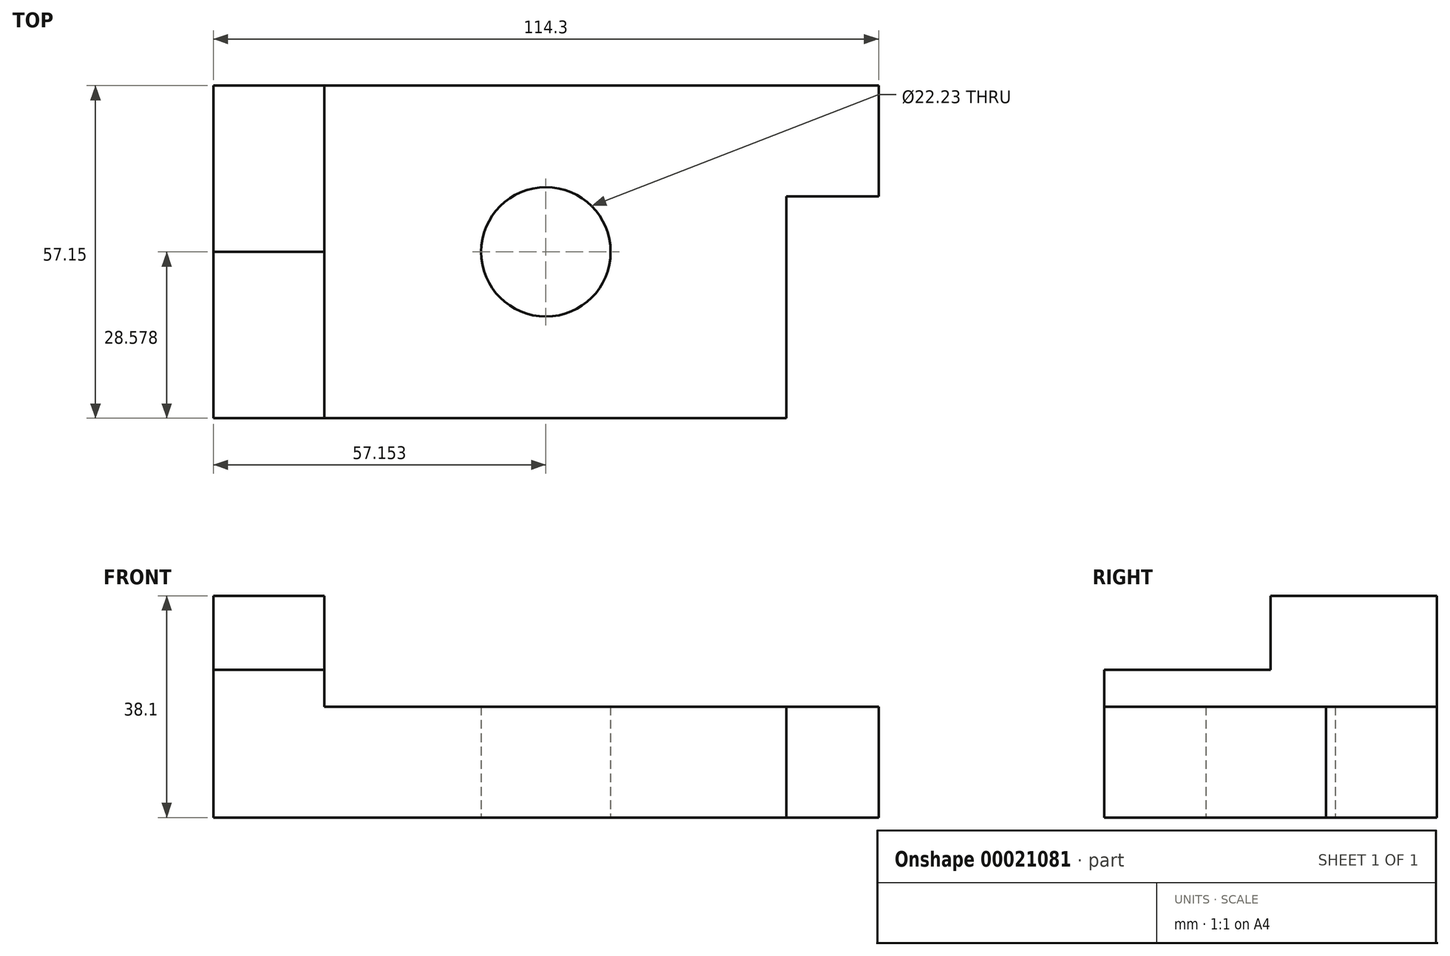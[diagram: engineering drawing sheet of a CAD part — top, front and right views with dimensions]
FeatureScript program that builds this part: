
annotation { "Feature Type Name" : "Feature", "Feature Type Description" : "" }
export const myFeature = defineFeature(function(context is Context, id is Id, definition is map)
    precondition{}
    {
        {
            var Q0;
            Q0=qCreatedBy(makeId("Top.planeOp"),FACE);
            var sketch = newSketch(context, id + "F0", { "sketchPlane" : qUnion([Q0])});
            skLineSegment(sketch, "E0.bottom", {"start": v(-56.1, 26.45) * mm, "end": v(58.2, 26.45) * mm});
            skLineSegment(sketch, "E0.top", {"start": v(-56.1, -30.7) * mm, "end": v(42.32, -30.7) * mm});
            skLineSegment(sketch, "E0.left", {"start": v(-56.1, 26.45) * mm, "end": v(-56.1, -30.7) * mm});
            skLineSegment(sketch, "E0.right", {"start": v(58.2, 26.45) * mm, "end": v(58.2, 7.4) * mm});
            skLineSegment(sketch, "E1.top", {"start": v(58.2, 7.4) * mm, "end": v(42.32, 7.4) * mm});
            skLineSegment(sketch, "E1.right", {"start": v(42.32, -30.7) * mm, "end": v(42.32, 7.4) * mm});
            skCircle(sketch, "E2", {"center": v(1.04, -2.12) * mm, "radius": 11.11 * mm});
            skPoint(sketch, "E3.orphan", {"position": v(58.2, -30.7) * mm});
            skSolve(sketch);
        }
        {
            var Q0;
            Q0 = qSketchRegion(id + "F0", true);
            extrude(context, id + "F1", {"entities" : qUnion([Q0]), "depth" : 38.1 * mm});
        }
        {
            var Q0;
            Q0=makeQuery(id+"F1.opExtrude","CAP_FACE",FACE,{"disambiguationData":[OSD([sQuery(id+"F0.wireOp",EDGE,"E0.bottom"),sQuery(id+"F0.wireOp",EDGE,"E0.top"),sQuery(id+"F0.wireOp",EDGE,"E0.left"),sQuery(id+"F0.wireOp",EDGE,"E0.right"),sQuery(id+"F0.wireOp",EDGE,"E1.top"),sQuery(id+"F0.wireOp",EDGE,"E1.right"),sQuery(id+"F0.wireOp",EDGE,"E2")])],"isStart":false});
            var sketch = newSketch(context, id + "F2", { "sketchPlane" : qUnion([Q0])});
            skLineSegment(sketch, "E4.bottom", {"start": v(-56.1, -30.7) * mm, "end": v(-37.06, -30.7) * mm});
            skLineSegment(sketch, "E4.top", {"start": v(-56.1, -2.12) * mm, "end": v(-37.06, -2.12) * mm});
            skLineSegment(sketch, "E4.left", {"start": v(-56.1, -30.7) * mm, "end": v(-56.1, -2.12) * mm});
            skLineSegment(sketch, "E4.right", {"start": v(-37.06, -30.7) * mm, "end": v(-37.06, -2.12) * mm});
            skSolve(sketch);
        }
        {
            var Q0;
            Q0 = qSketchRegion(id + "F2", true);
            extrude(context, id + "F3", {"entities" : qUnion([Q0]), "operationType" : NewBodyOperationType.REMOVE, "oppositeDirection" : true, "depth" : 12.7 * mm});
        }
        {
            var Q0;
            Q0=makeQuery(id+"F1.opExtrude","CAP_FACE",FACE,{"disambiguationData":[OSD([sQuery(id+"F0.wireOp",EDGE,"E0.bottom"),sQuery(id+"F0.wireOp",EDGE,"E0.top"),sQuery(id+"F0.wireOp",EDGE,"E0.left"),sQuery(id+"F0.wireOp",EDGE,"E0.right"),sQuery(id+"F0.wireOp",EDGE,"E1.top"),sQuery(id+"F0.wireOp",EDGE,"E1.right"),sQuery(id+"F0.wireOp",EDGE,"E2")])],"isStart":false});
            var sketch = newSketch(context, id + "F4", { "sketchPlane" : qUnion([Q0])});
            skLineSegment(sketch, "E5.bottom", {"start": v(58.2, 7.4) * mm, "end": v(42.32, 7.4) * mm});
            skLineSegment(sketch, "E5.top", {"start": v(58.2, 26.45) * mm, "end": v(42.32, 26.45) * mm});
            skLineSegment(sketch, "E5.left", {"start": v(58.2, 7.4) * mm, "end": v(58.2, 26.45) * mm});
            skLineSegment(sketch, "E5.right", {"start": v(42.32, 7.4) * mm, "end": v(42.32, 26.45) * mm});
            skSolve(sketch);
        }
        {
            var Q0;
            Q0 = qSketchRegion(id + "F4", true);
            extrude(context, id + "F5", {"entities" : qUnion([Q0]), "operationType" : NewBodyOperationType.REMOVE, "oppositeDirection" : true, "depth" : 19.05 * mm});
        }
        {
            var Q0;
            Q0=makeQuery(id+"F1.opExtrude","CAP_FACE",FACE,{"disambiguationData":[OSD([sQuery(id+"F0.wireOp",EDGE,"E0.bottom"),sQuery(id+"F0.wireOp",EDGE,"E0.top"),sQuery(id+"F0.wireOp",EDGE,"E0.left"),sQuery(id+"F0.wireOp",EDGE,"E0.right"),sQuery(id+"F0.wireOp",EDGE,"E1.top"),sQuery(id+"F0.wireOp",EDGE,"E1.right"),sQuery(id+"F0.wireOp",EDGE,"E2")])],"isStart":false});
            var sketch = newSketch(context, id + "F6", { "sketchPlane" : qUnion([Q0])});
            skLineSegment(sketch, "E6.bottom", {"start": v(42.32, -30.7) * mm, "end": v(-37.06, -30.7) * mm});
            skLineSegment(sketch, "E6.top", {"start": v(42.32, 26.45) * mm, "end": v(-37.06, 26.45) * mm});
            skLineSegment(sketch, "E6.left", {"start": v(42.32, -30.7) * mm, "end": v(42.32, 26.45) * mm});
            skLineSegment(sketch, "E6.right", {"start": v(-37.06, -30.7) * mm, "end": v(-37.06, 26.45) * mm});
            skSolve(sketch);
        }
        {
            var Q0;
            Q0 = qSketchRegion(id + "F6", true);
            extrude(context, id + "F7", {"entities" : qUnion([Q0]), "operationType" : NewBodyOperationType.REMOVE, "oppositeDirection" : true, "depth" : 19.05 * mm});
        }
    });
